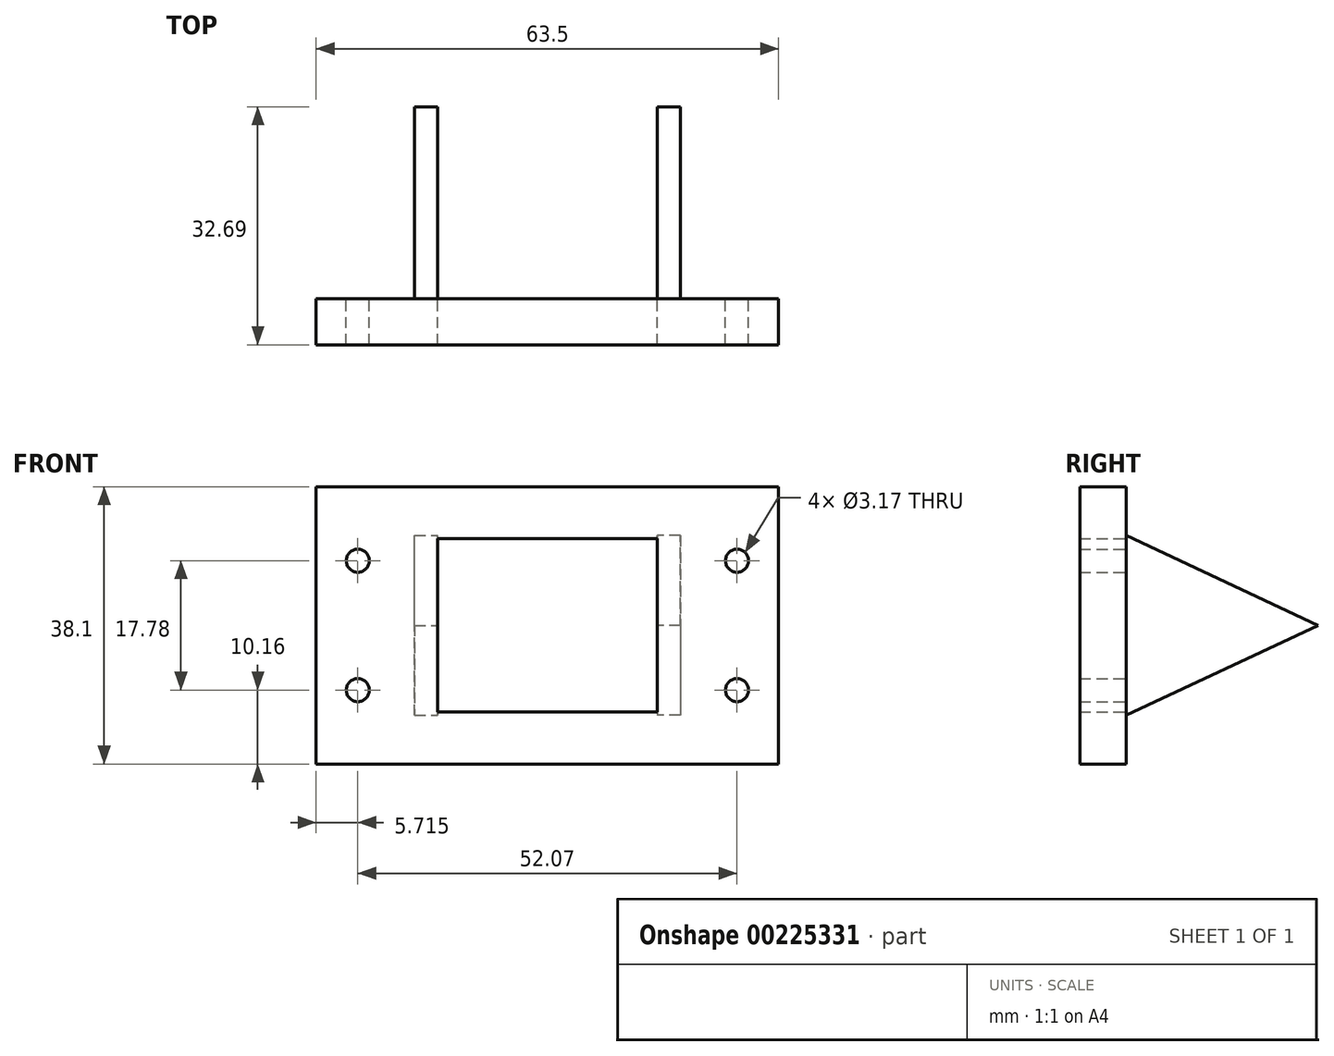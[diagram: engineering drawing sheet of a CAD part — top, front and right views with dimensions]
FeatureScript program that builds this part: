
annotation { "Feature Type Name" : "Feature", "Feature Type Description" : "" }
export const myFeature = defineFeature(function(context is Context, id is Id, definition is map)
    precondition{}
    {
        {
            var Q0;
            Q0=qCreatedBy(makeId("Front.planeOp"),FACE);
            var sketch = newSketch(context, id + "F0", { "sketchPlane" : qUnion([Q0])});
            skLineSegment(sketch, "E0.bottom", {"start": v(0, 0) * mm, "end": v(63.5, 0) * mm});
            skLineSegment(sketch, "E0.top", {"start": v(0, 38.1) * mm, "end": v(63.5, 38.1) * mm});
            skLineSegment(sketch, "E0.left", {"start": v(0, 0) * mm, "end": v(0, 38.1) * mm});
            skLineSegment(sketch, "E0.right", {"start": v(63.5, 0) * mm, "end": v(63.5, 38.1) * mm});
            skCircle(sketch, "E1", {"center": v(5.71, 27.94) * mm, "radius": 1.59 * mm});
            skCircle(sketch, "E2", {"center": v(57.79, 27.94) * mm, "radius": 1.59 * mm});
            skCircle(sketch, "E3", {"center": v(57.79, 10.16) * mm, "radius": 1.59 * mm});
            skCircle(sketch, "E4", {"center": v(5.71, 10.16) * mm, "radius": 1.59 * mm});
            skPoint(sketch, "E5.start.orphan", {"position": v(31.75, 27.94) * mm});
            skPoint(sketch, "E6.end.orphan", {"position": v(5.72, 19.05) * mm});
            skPoint(sketch, "E6.start.orphan", {"position": v(0, 19.05) * mm});
            skPoint(sketch, "E7.end.orphan", {"position": v(31.19, 0) * mm});
            skPoint(sketch, "E7.start.orphan", {"position": v(31.75, 10.16) * mm});
            skPoint(sketch, "E8.end.orphan", {"position": v(63.5, 19.05) * mm});
            skPoint(sketch, "E9.orphan", {"position": v(57.79, 19.05) * mm});
            skLineSegment(sketch, "E10.bottom", {"start": v(16.67, 30.96) * mm, "end": v(46.83, 30.96) * mm});
            skLineSegment(sketch, "E10.top", {"start": v(16.67, 7.14) * mm, "end": v(46.83, 7.14) * mm});
            skLineSegment(sketch, "E10.left", {"start": v(16.67, 30.96) * mm, "end": v(16.67, 7.14) * mm});
            skLineSegment(sketch, "E10.right", {"start": v(46.83, 30.96) * mm, "end": v(46.83, 7.14) * mm});
            skPoint(sketch, "E11.start.orphan", {"position": v(31.75, 38.1) * mm});
            skLineSegment(sketch, "E12", {"start": v(31.06, 30.96) * mm, "end": v(31.06, 38.1) * mm});
            skLineSegment(sketch, "E13", {"start": v(16.67, 19.05) * mm, "end": v(0, 19.05) * mm});
            skLineSegment(sketch, "E14", {"start": v(46.83, 22.52) * mm, "end": v(63.5, 22.52) * mm});
            skLineSegment(sketch, "E15", {"start": v(27.63, 7.14) * mm, "end": v(27.63, 0) * mm});
            skSolve(sketch);
        }
        {
            var Q0;
            Q0=qSketchRegion(id+"F0",true);
            extrude(context, id + "F1", {"entities" : qUnion([Q0]), "depth" : 6.35 * mm});
        }
        {
            var Q0;
            Q0=makeQuery(id+"F1.opExtrude","SWEPT_FACE",FACE,{"disambiguationData":[OSD([sQuery(id+"F0.wireOp",EDGE,"E10.left")])]});
            var sketch = newSketch(context, id + "F2", { "sketchPlane" : qUnion([Q0])});
            skLineSegment(sketch, "E16.0", {"start": v(0.17, 31.32) * mm, "end": v(25.56, 19.41) * mm});
            skLineSegment(sketch, "E17.0", {"start": v(25.57, 18.69) * mm, "end": v(0.17, 6.78) * mm});
            skLineSegment(sketch, "E18", {"start": v(0.17, 6.78) * mm, "end": v(0, 6.7) * mm});
            skLineSegment(sketch, "E19", {"start": v(0, 6.7) * mm, "end": v(0, 7.14) * mm});
            skLineSegment(sketch, "E20", {"start": v(0.17, 31.32) * mm, "end": v(0, 31.4) * mm});
            skLineSegment(sketch, "E21", {"start": v(0, 31.4) * mm, "end": v(0, 30.96) * mm});
            skLineSegment(sketch, "E22", {"start": v(25.57, 18.69) * mm, "end": v(26.34, 19.05) * mm});
            skLineSegment(sketch, "E23", {"start": v(26.34, 19.05) * mm, "end": v(25.56, 19.41) * mm});
            skPoint(sketch, "E24.start.orphan", {"position": v(25.4, 19.05) * mm});
            skLineSegment(sketch, "E25", {"start": v(0, 6.7) * mm, "end": v(0, 31.4) * mm});
            skSolve(sketch);
        }
        {
            var Q0;
            Q0 = qSketchRegion(id + "F2", true);
            extrude(context, id + "F3", {"entities" : qUnion([Q0]), "operationType" : NewBodyOperationType.ADD, "oppositeDirection" : true, "depth" : 3.17 * mm});
        }
        {
            var Q0;
            Q0=makeQuery(id+"F1.opExtrude","SWEPT_FACE",FACE,{"disambiguationData":[OSD([sQuery(id+"F0.wireOp",EDGE,"E10.right")])]});
            var sketch = newSketch(context, id + "F4", { "sketchPlane" : qUnion([Q0])});
            skLineSegment(sketch, "E26.0.1", {"start": v(-26.34, 19.05) * mm, "end": v(-0.17, 6.78) * mm});
            skLineSegment(sketch, "E26.0.2", {"start": v(-0.17, 31.32) * mm, "end": v(-26.34, 19.05) * mm});
            skLineSegment(sketch, "E27", {"start": v(-0.17, 31.32) * mm, "end": v(0, 31.4) * mm});
            skLineSegment(sketch, "E28", {"start": v(0, 31.4) * mm, "end": v(0, 6.7) * mm});
            skLineSegment(sketch, "E29", {"start": v(0, 6.7) * mm, "end": v(-0.17, 6.78) * mm});
            skSolve(sketch);
        }
        {
            var Q0;
            Q0 = qSketchRegion(id + "F4", true);
            extrude(context, id + "F5", {"entities" : qUnion([Q0]), "operationType" : NewBodyOperationType.ADD, "oppositeDirection" : true, "depth" : 3.17 * mm});
        }
    });
